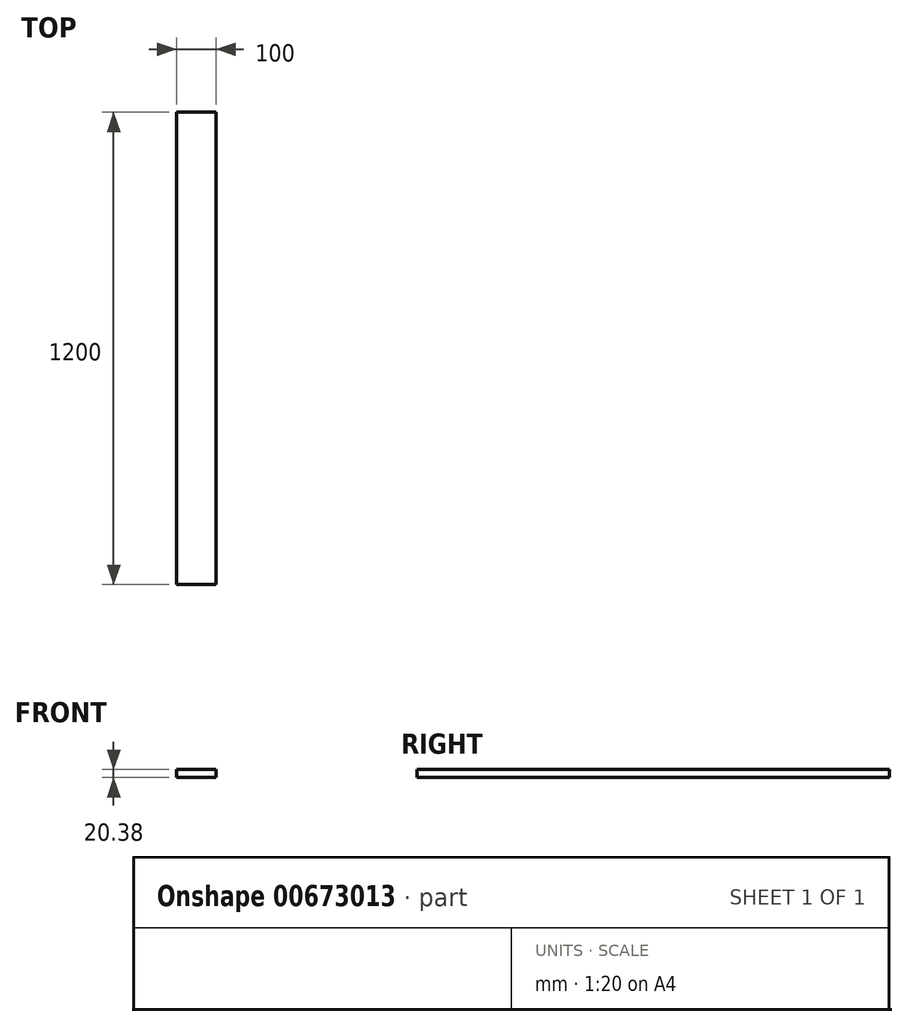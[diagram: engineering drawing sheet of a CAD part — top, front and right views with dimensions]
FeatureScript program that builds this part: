
annotation { "Feature Type Name" : "Feature", "Feature Type Description" : "" }
export const myFeature = defineFeature(function(context is Context, id is Id, definition is map)
    precondition{}
    {
        {
            var Q0;
            Q0=qCreatedBy(makeId("Front.planeOp"),FACE);
            var sketch = newSketch(context, id + "F0", { "sketchPlane" : qUnion([Q0])});
            skLineSegment(sketch, "E0.bottom", {"start": v(0, 0) * mm, "end": v(45.1, 0) * mm});
            skLineSegment(sketch, "E0.top", {"start": v(0, 20.38) * mm, "end": v(45.1, 20.38) * mm});
            skLineSegment(sketch, "E0.left", {"start": v(0, 0) * mm, "end": v(0, 20.38) * mm});
            skLineSegment(sketch, "E0.right", {"start": v(45.1, 0) * mm, "end": v(45.1, 20.38) * mm});
            skSolve(sketch);
        }
        {
            var Q0;
            Q0=makeQuery(id+"F0.imprint","IMPRINT",FACE,{"disambiguationData":[TD([[makeQuery(id+"F0.imprint","IMPRINT",EDGE,{"derivedFrom":sQuery(id+"F0.wireOp",EDGE,"E0.bottom")}),1.0]])]});
            extrude(context, id + "F1", {"entities" : qUnion([Q0]), "depth" : 1200 * mm, "offsetDistance" : 25 * mm});
        }
        {
            var Q0;
            Q0=makeQuery(id+"F1.opExtrude","SWEPT_FACE",FACE,{"disambiguationData":[OSD([sQuery(id+"F0.wireOp",EDGE,"E0.bottom")])]});
            extrude(context, id + "F2", {"entities" : qUnion([Q0]), "operationType" : NewBodyOperationType.ADD, "oppositeDirection" : true, "depth" : 20 * mm, "offsetDistance" : 25 * mm});
        }
        {
            var Q0;
            Q0=makeQuery(id+"F1.opExtrude","SWEPT_FACE",FACE,{"disambiguationData":[OSD([sQuery(id+"F0.wireOp",EDGE,"E0.left")])]});
            extrude(context, id + "F3", {"entities" : qUnion([Q0]), "operationType" : NewBodyOperationType.ADD, "oppositeDirection" : true, "depth" : 100 * mm, "offsetDistance" : 25 * mm});
        }
        {
            var Q0;
            {var subQ0=sQuery(id+"F0.wireOp",EDGE,"E0.bottom");Q0=makeQuery(id+"F3.boolean.opBoolean","MERGE",FACE,{"derivedFrom":[makeQuery(id+"F1.opExtrude","SWEPT_FACE",FACE,{"disambiguationData":[OSD([subQ0])]}),makeQuery(id+"F3.opExtrude","SWEPT_FACE",FACE,{"disambiguationData":[OSD([subQ0,sQuery(id+"F0.wireOp",EDGE,"E0.left")])]})]});}
            extrude(context, id + "F4", {"entities" : qUnion([Q0]), "operationType" : NewBodyOperationType.INTERSECT, "oppositeDirection" : true, "depth" : 200 * mm, "offsetDistance" : 25 * mm});
        }
    });
